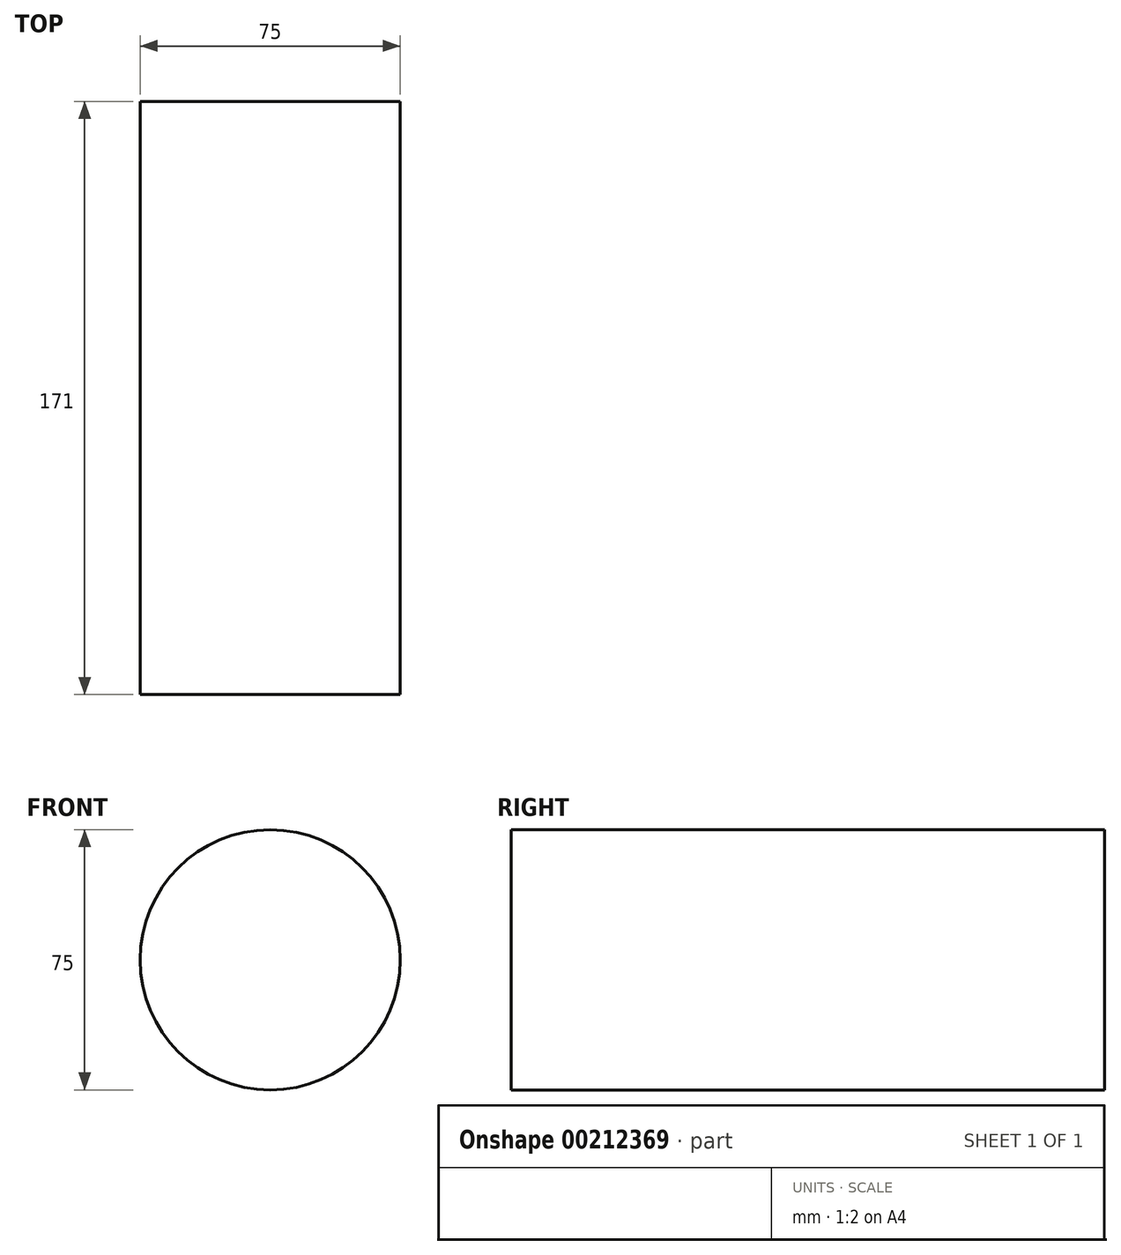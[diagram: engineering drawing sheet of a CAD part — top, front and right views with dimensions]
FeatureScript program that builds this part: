
annotation { "Feature Type Name" : "Feature", "Feature Type Description" : "" }
export const myFeature = defineFeature(function(context is Context, id is Id, definition is map)
    precondition{}
    {
        {
            var Q0;
            Q0=qCreatedBy(makeId("Front.planeOp"),FACE);
            var sketch = newSketch(context, id + "F0", { "sketchPlane" : qUnion([Q0])});
            skCircle(sketch, "E0", {"center": v(0, 0) * mm, "radius": 37.5 * mm});
            skSolve(sketch);
        }
        {
            var Q0;
            Q0=makeQuery(id+"F0.imprint","IMPRINT",FACE,{"disambiguationData":[TD([[makeQuery(id+"F0.imprint","IMPRINT",EDGE,{"derivedFrom":sQuery(id+"F0.wireOp",EDGE,"E0")}),1.0]])]});
            extrude(context, id + "F1", {"entities" : qUnion([Q0]), "depth" : 171 * mm});
        }
    });
